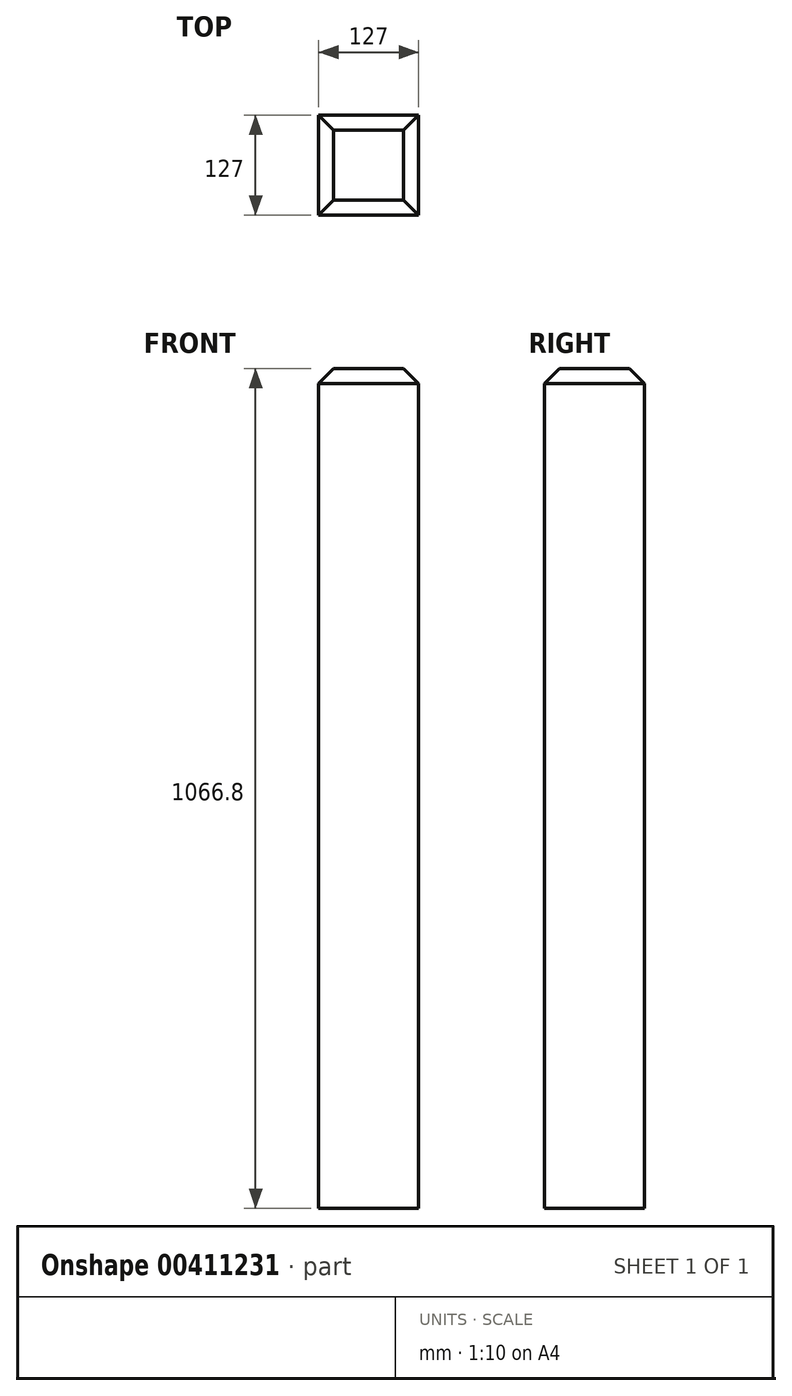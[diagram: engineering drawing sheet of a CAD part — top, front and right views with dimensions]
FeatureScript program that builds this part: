
annotation { "Feature Type Name" : "Feature", "Feature Type Description" : "" }
export const myFeature = defineFeature(function(context is Context, id is Id, definition is map)
    precondition{}
    {
        {
            var Q0;
            Q0=qCreatedBy(makeId("Top.planeOp"),FACE);
            var sketch = newSketch(context, id + "F0", { "sketchPlane" : qUnion([Q0])});
            skLineSegment(sketch, "E0.bottom", {"start": v(-63.5, 63.5) * mm, "end": v(63.5, 63.5) * mm});
            skLineSegment(sketch, "E0.top", {"start": v(-63.5, -63.5) * mm, "end": v(63.5, -63.5) * mm});
            skLineSegment(sketch, "E0.left", {"start": v(-63.5, 63.5) * mm, "end": v(-63.5, -63.5) * mm});
            skLineSegment(sketch, "E0.right", {"start": v(63.5, 63.5) * mm, "end": v(63.5, -63.5) * mm});
            skPoint(sketch, "E0.middle", {"position": v(0, 0) * mm});
            skSolve(sketch);
        }
        {
            var Q0;
            Q0=makeQuery(id+"F0.imprint","IMPRINT",FACE,{"disambiguationData":[TD([[makeQuery(id+"F0.imprint","IMPRINT",EDGE,{"derivedFrom":sQuery(id+"F0.wireOp",EDGE,"E0.bottom")}),-1.0]])]});
            extrude(context, id + "F1", {"entities" : qUnion([Q0]), "depth" : 1066.8 * mm});
        }
        {
            var Q0;
            Q0=makeQuery(id+"F1.opExtrude","CAP_EDGE",EDGE,{"disambiguationData":[OSD([sQuery(id+"F0.wireOp",EDGE,"E0.top")])],"isStart":false});
            var Q1;
            Q1=makeQuery(id+"F1.opExtrude","CAP_EDGE",EDGE,{"disambiguationData":[OSD([sQuery(id+"F0.wireOp",EDGE,"E0.left")])],"isStart":false});
            var Q2;
            Q2=makeQuery(id+"F1.opExtrude","CAP_EDGE",EDGE,{"disambiguationData":[OSD([sQuery(id+"F0.wireOp",EDGE,"E0.bottom")])],"isStart":false});
            var Q3;
            Q3=makeQuery(id+"F1.opExtrude","CAP_EDGE",EDGE,{"disambiguationData":[OSD([sQuery(id+"F0.wireOp",EDGE,"E0.right")])],"isStart":false});
            chamfer(context, id + "F2", {"entities" : qUnion([Q0, Q1, Q2, Q3]), "width" : 19.05 * mm, "tangentPropagation" : true});
        }
    });
